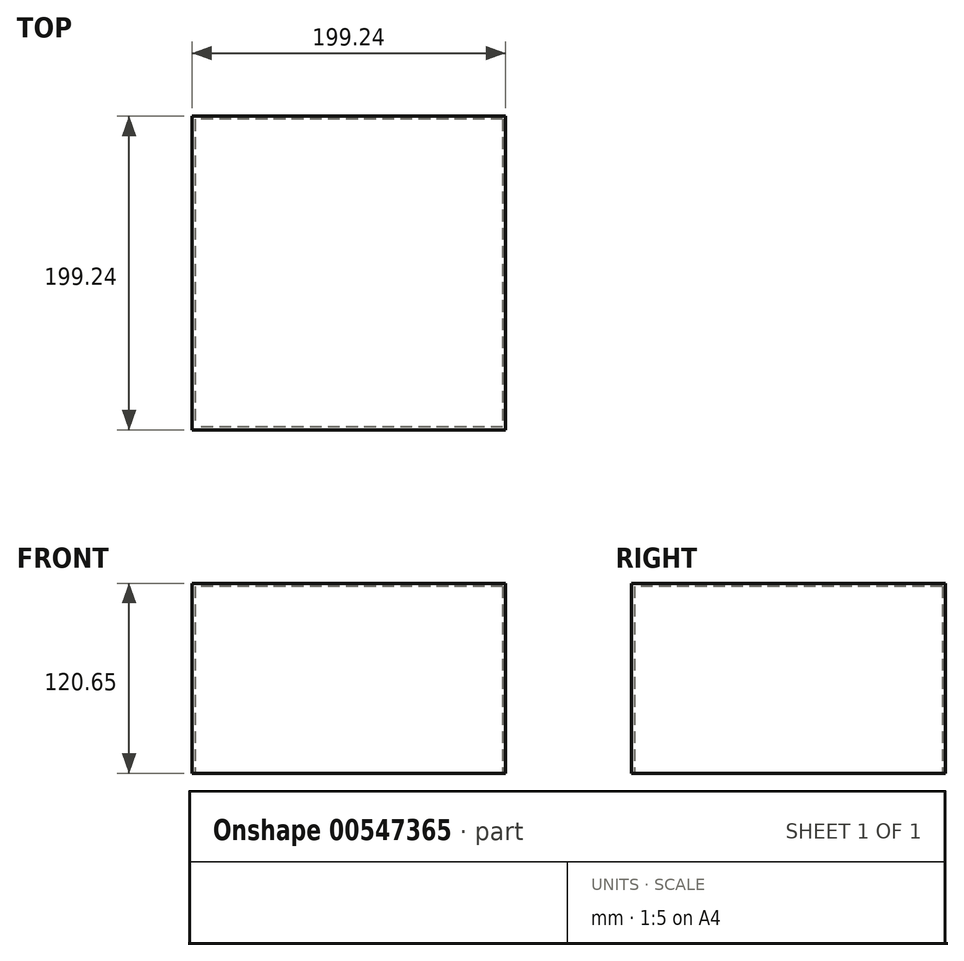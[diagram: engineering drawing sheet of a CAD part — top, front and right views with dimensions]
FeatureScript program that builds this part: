
annotation { "Feature Type Name" : "Feature", "Feature Type Description" : "" }
export const myFeature = defineFeature(function(context is Context, id is Id, definition is map)
    precondition{}
    {
        {
            var Q0;
            Q0=qCreatedBy(makeId("Top.planeOp"),FACE);
            var sketch = newSketch(context, id + "F0", { "sketchPlane" : qUnion([Q0])});
            skLineSegment(sketch, "E0.bottom", {"start": v(99.62, 99.62) * mm, "end": v(-99.62, 99.62) * mm});
            skLineSegment(sketch, "E0.top", {"start": v(99.62, -99.62) * mm, "end": v(-99.62, -99.62) * mm});
            skLineSegment(sketch, "E0.left", {"start": v(99.62, 99.62) * mm, "end": v(99.62, -99.62) * mm});
            skLineSegment(sketch, "E0.right", {"start": v(-99.62, 99.62) * mm, "end": v(-99.62, -99.62) * mm});
            skPoint(sketch, "E0.middle", {"position": v(0, 0) * mm});
            skSolve(sketch);
        }
        {
            var Q0;
            Q0 = qSketchRegion(id + "F0", true);
            extrude(context, id + "F1", {"entities" : qUnion([Q0]), "depth" : 120.65 * mm, "offsetDistance" : 25.4 * mm});
        }
        {
            var Q0;
            Q0=makeQuery(id+"F1.opExtrude","CAP_FACE",FACE,{"disambiguationData":[OSD([sQuery(id+"F0.wireOp",EDGE,"E0.bottom"),sQuery(id+"F0.wireOp",EDGE,"E0.top"),sQuery(id+"F0.wireOp",EDGE,"E0.left"),sQuery(id+"F0.wireOp",EDGE,"E0.right")])],"isStart":true});
            shell(context, id + "F2", {"entities" : qUnion([Q0]), "thickness" : 1.9 * mm});
        }
    });
